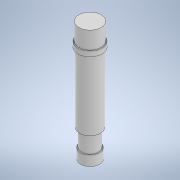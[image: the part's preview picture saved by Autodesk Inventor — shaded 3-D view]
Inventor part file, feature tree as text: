
AUTODESK INVENTOR PART (.ipt)
format: ipt  version: 2021.1 (Build 251245000, 245)  size: 121,344 bytes
history: native  units: in
note: dims shown in document units (in); Inventor stores cm internally (conversion verified against a paired STEP export)
features: revolve x1, sketch x1
ambient origin geometry x8: Origin, YZ Plane, XZ Plane, XY Plane, X Axis, Y Axis, Z Axis, Center Point
bodies: Solid1 (feature_tree)
feature tree (2):
  revolve  "Revolution1"  [1 undecoded]
  sketch  "Sketch1"  dims[d0=0.86in d1=0.55in d2=0.25in d3=0.6in d4=0.5175in d5=3.45in d7=0.4225in d8=0.86in d9=0.47in d10=0.5in d12=90.0deg]
note: 1 required parameter value undecoded (feature->parameter linkage not recoverable at this tier; creation-order binding heuristic only, values carry confidence <= 0.55)
